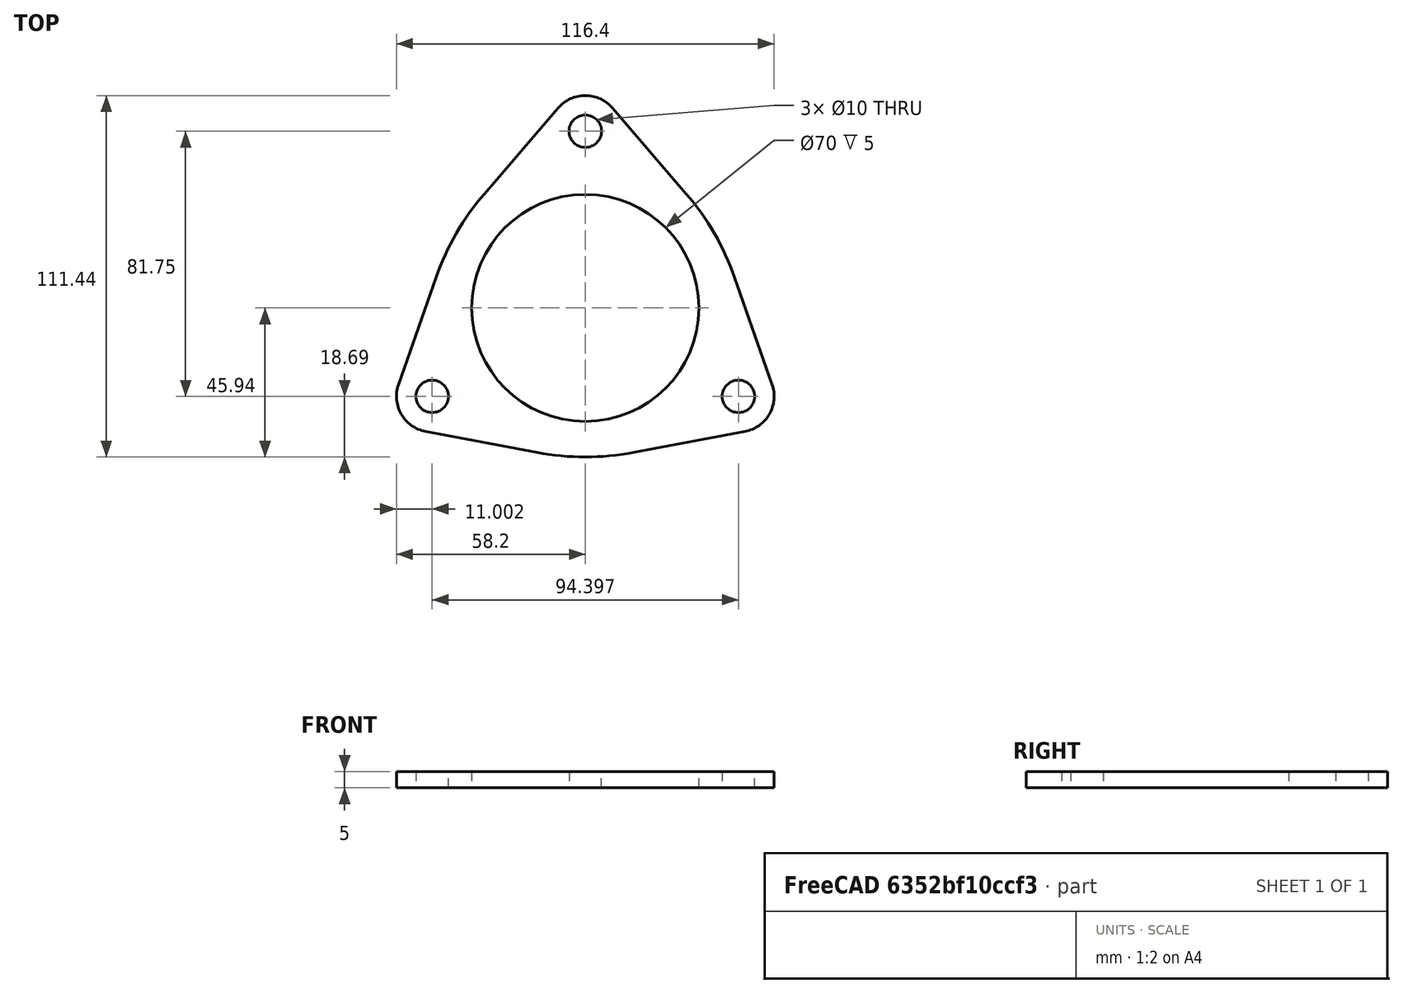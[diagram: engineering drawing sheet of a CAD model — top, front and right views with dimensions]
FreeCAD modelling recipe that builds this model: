
FCSTD DOCUMENT  (FreeCAD 0.20R29410 (Git))
Label: MangoJelly_Solutions_Tutorial_Ep4
License: All rights reserved
LicenseURL: http://en.wikipedia.org/wiki/All_rights_reserved
objects: Image::ImagePlane×1, Sketcher::SketchObject×1, PartDesign::Pad×1, PartDesign::Body×1
note: 4 computed .brp shape members not serialized (recipe doc carries the construction recipe); baked Part::Feature solids carry a one-line shape summary decoded from their .brp

FEATURE [Image::ImagePlane] ImagePlane
  Placement = pos=(1,9,0) rot=(0,0,1;0rad)
  XSize = 128.911
  YSize = 123.688
FEATURE [Sketcher::SketchObject] Sketch
  FullyConstrained = true
  sketch-geometry (19):
    g0: Circle CenterX=0 CenterY=0 CenterZ=0 NormalX=0 NormalY=0 NormalZ=1 AngleXU=0 Radius=35
    g1: Circle CenterX=-47.1984 CenterY=-27.25 CenterZ=0 NormalX=0 NormalY=0 NormalZ=1 AngleXU=0 Radius=5
    g2: LineSegment StartX=0 StartY=0 StartZ=0 EndX=-47.1984 EndY=-27.25 EndZ=0
    g3: Circle CenterX=47.1984 CenterY=-27.25 CenterZ=0 NormalX=0 NormalY=0 NormalZ=1 AngleXU=0 Radius=5
    g4: LineSegment StartX=0 StartY=0 StartZ=0 EndX=47.1984 EndY=-27.25 EndZ=0
    g5: Circle CenterX=-5.3e-15 CenterY=54.5 CenterZ=0 NormalX=0 NormalY=0 NormalZ=1 AngleXU=0 Radius=5
    g6: LineSegment StartX=0 StartY=0 StartZ=0 EndX=-5.3e-15 EndY=54.5 EndZ=0
    g7: ArcOfCircle CenterX=-5.3e-15 CenterY=54.5 CenterZ=0 NormalX=0 NormalY=0 NormalZ=1 AngleXU=0 Radius=11 StartAngle=0.710283 EndAngle=2.43131
    g8: LineSegment StartX=8.33995 StartY=61.6725 StartZ=0 EndX=31.1616 EndY=35.1363 EndZ=0
    g9: ArcOfCircle CenterX=47.1984 CenterY=-27.25 CenterZ=0 NormalX=0 NormalY=0 NormalZ=1 AngleXU=0 Radius=11 StartAngle=4.89907 EndAngle=6.6201
    g10: LineSegment StartX=57.58 StartY=-23.6137 StartZ=0 EndX=46.0098 EndY=9.41861 EndZ=0
    g11: ArcOfCircle CenterX=-29.4926 CenterY=-17.0275 CenterZ=0 NormalX=0 NormalY=0 NormalZ=1 AngleXU=0 Radius=80 StartAngle=0.336915 EndAngle=0.710283
    g12: ArcOfCircle CenterX=29.4926 CenterY=-17.0275 CenterZ=0 NormalX=0 NormalY=0 NormalZ=1 AngleXU=0 Radius=80 StartAngle=2.43131 EndAngle=2.80468
    g13: LineSegment StartX=-8.33995 StartY=61.6725 StartZ=0 EndX=-31.1616 EndY=35.1363 EndZ=0
    g14: LineSegment StartX=-46.0098 StartY=9.41861 StartZ=0 EndX=-57.58 EndY=-23.6137 EndZ=0
    g15: ArcOfCircle CenterX=0 CenterY=34.0551 CenterZ=0 NormalX=0 NormalY=0 NormalZ=1 AngleXU=0 Radius=80 StartAngle=4.5257 EndAngle=4.89907
    g16: LineSegment StartX=14.8481 StartY=-44.5549 StartZ=0 EndX=49.24 EndY=-38.0589 EndZ=0
    g17: LineSegment StartX=-14.8481 StartY=-44.5549 StartZ=0 EndX=-49.24 EndY=-38.0589 EndZ=0
    g18: ArcOfCircle CenterX=-47.1984 CenterY=-27.25 CenterZ=0 NormalX=0 NormalY=0 NormalZ=1 AngleXU=0 Radius=11 StartAngle=2.80468 EndAngle=4.5257
  constraints (44):
    c: Coincident(g0,g-1)
    c: Diameter(g0) = 70
    c: Diameter(g1) = 10
    c: Coincident(g2,g0)
    c: Coincident(g2,g1)
    c: Coincident(g4,g0)
    c: Coincident(g4,g3)
    c: Angle(g2,g4) = 2.0944
    c: Equal(g2,g4)
    c: Equal(g1,g3)
    c: Equal(g1,g5)
    c: Coincident(g6,g0)
    c: Coincident(g6,g5)
    c: Angle(g4,g6) = 2.0944
    c: Equal(g6,g4)
    c: DistanceY(g6,g6) = 54.5
    c: Coincident(g7,g5)
    c: Symmetric(g7,g7,g-2)
    c: Radius(g7) = 11
    c: Tangent(g8,g7) = 1.5708
    c: Symmetric(g9,g9,g4)
    c: Tangent(g10,g9) = -1.5708
    c: Equal(g7,g9)
    c: Equal(g10,g8)
    c: Tangent(g11,g10) = -1.5708
    c: Tangent(g11,g8) = 1.5708
    c: Radius(g11) = 80
    c: PointOnObject(g15,g-2)
    c: Coincident(g16,g9)
    c: Coincident(g18,g1)
    c: Tangent(g18,g14) = -1.5708
    c: Tangent(g18,g17) = 1.5708
    c: Tangent(g17,g15) = 1.5708
    c: Tangent(g16,g15) = -1.5708
    c: Tangent(g14,g12) = -1.5708
    c: Tangent(g13,g12) = -1.5708
    c: Tangent(g13,g7) = -1.5708
    c: Equal(g18,g7)
    c: Equal(g8,g13)
    c: Equal(g13,g14)
    c: Equal(g14,g17)
    c: Equal(g17,g16)
    c: Distance(g8) = 35
    c: Equal(g15,g11)
FEATURE [PartDesign::Pad] Pad
  Direction = (0,0,1)
  Length = 5
  Length2 = 10
  Profile = -> Sketch
  ReferenceAxis = -> Sketch [N_Axis]
  Type = 0
FEATURE [PartDesign::Body] Body
  Group = -> [Sketch,Pad]
  Origin = -> Origin
  Tip = -> Pad
